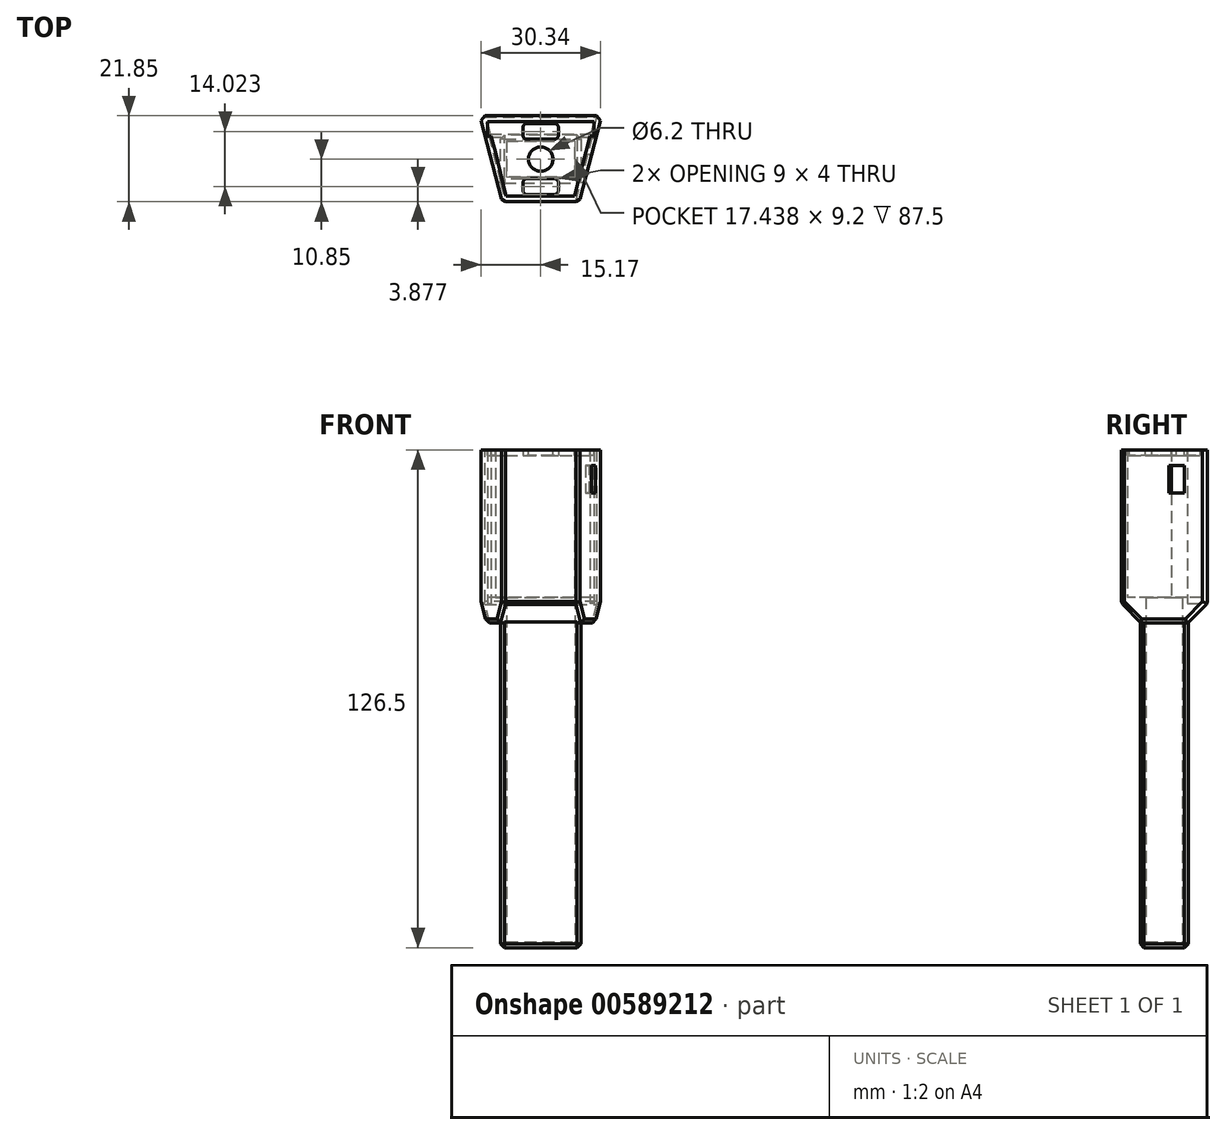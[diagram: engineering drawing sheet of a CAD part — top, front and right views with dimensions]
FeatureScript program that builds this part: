
annotation { "Feature Type Name" : "Feature", "Feature Type Description" : "" }
export const myFeature = defineFeature(function(context is Context, id is Id, definition is map)
    precondition{}
    {
        {
            var Q0;
            Q0=qCreatedBy(makeId("Top.planeOp"),FACE);
            var sketch = newSketch(context, id + "F0", { "sketchPlane" : qUnion([Q0])});
            skLineSegment(sketch, "E0", {"start": v(0, 11) * mm, "end": v(15.5, 11) * mm});
            skLineSegment(sketch, "E1", {"start": v(9.75, -10.85) * mm, "end": v(0, -10.85) * mm});
            skLineSegment(sketch, "E2", {"start": v(-9.75, -10.85) * mm, "end": v(0, -10.85) * mm});
            skLineSegment(sketch, "E3", {"start": v(-15.5, 11) * mm, "end": v(0, 11) * mm});
            skLineSegment(sketch, "E4", {"start": v(15.5, 11) * mm, "end": v(9.75, -10.85) * mm});
            skLineSegment(sketch, "E5", {"start": v(-15.5, 11) * mm, "end": v(-9.75, -10.85) * mm});
            skLineSegment(sketch, "E6", {"start": v(0, 9.5) * mm, "end": v(-15.1, 9.5) * mm});
            skLineSegment(sketch, "E7", {"start": v(0, 9.5) * mm, "end": v(15.1, 9.5) * mm});
            skLineSegment(sketch, "E8", {"start": v(0, -9.35) * mm, "end": v(-10.14, -9.35) * mm});
            skLineSegment(sketch, "E9", {"start": v(0, -9.35) * mm, "end": v(10.14, -9.35) * mm});
            skLineSegment(sketch, "E10", {"start": v(-11.54, 1.84) * mm, "end": v(-13.55, 9.5) * mm});
            skLineSegment(sketch, "E11", {"start": v(11.74, 2.61) * mm, "end": v(13.55, 9.5) * mm});
            skLineSegment(sketch, "E12", {"start": v(8.72, 0) * mm, "end": v(8.72, 4.6) * mm});
            skLineSegment(sketch, "E13", {"start": v(8.72, 4.6) * mm, "end": v(0, 4.6) * mm});
            skLineSegment(sketch, "E14.MirrorCS", {"start": v(-8.72, 0) * mm, "end": v(-8.72, 4.6) * mm});
            skLineSegment(sketch, "E15.MirrorCS", {"start": v(-8.72, 4.6) * mm, "end": v(0, 4.6) * mm});
            skLineSegment(sketch, "E16.MirrorCS", {"start": v(-8.72, 0) * mm, "end": v(-8.72, -4.6) * mm});
            skLineSegment(sketch, "E17.MirrorCS", {"start": v(-8.72, -4.6) * mm, "end": v(0, -4.6) * mm});
            skLineSegment(sketch, "E18.MirrorCS", {"start": v(8.72, -4.6) * mm, "end": v(0, -4.6) * mm});
            skLineSegment(sketch, "E19.MirrorCS", {"start": v(8.72, 0) * mm, "end": v(8.72, -4.6) * mm});
            skLineSegment(sketch, "E20", {"start": v(0, 4.6) * mm, "end": v(0, 6.1) * mm});
            skLineSegment(sketch, "E21", {"start": v(0, 6.1) * mm, "end": v(-8.72, 6.1) * mm});
            skLineSegment(sketch, "E22", {"start": v(-8.72, 6.1) * mm, "end": v(-10.22, 6.1) * mm});
            skLineSegment(sketch, "E23", {"start": v(-10.22, 6.1) * mm, "end": v(-10.22, -4.6) * mm});
            skLineSegment(sketch, "E24", {"start": v(-10.22, -4.6) * mm, "end": v(-10.22, -6.1) * mm});
            skLineSegment(sketch, "E25", {"start": v(0, 4.6) * mm, "end": v(0, 0) * mm, "construction": true});
            skLineSegment(sketch, "E26", {"start": v(0, 0) * mm, "end": v(-8.72, 0) * mm, "construction": true});
            skLineSegment(sketch, "E27", {"start": v(-10.22, -6.1) * mm, "end": v(0, -6.1) * mm});
            skLineSegment(sketch, "E28.MirrorCS", {"start": v(0, 6.1) * mm, "end": v(8.72, 6.1) * mm});
            skLineSegment(sketch, "E29.MirrorCS", {"start": v(8.72, 6.1) * mm, "end": v(10.22, 6.1) * mm});
            skLineSegment(sketch, "E30.MirrorCS", {"start": v(10.22, 6.1) * mm, "end": v(10.22, -4.6) * mm});
            skLineSegment(sketch, "E31.MirrorCS", {"start": v(10.22, -4.6) * mm, "end": v(10.22, -6.1) * mm});
            skLineSegment(sketch, "E32.MirrorCS", {"start": v(10.22, -6.1) * mm, "end": v(0, -6.1) * mm});
            skLineSegment(sketch, "E33", {"start": v(0, -4.6) * mm, "end": v(0, -9.35) * mm, "construction": true});
            skLineSegment(sketch, "E34", {"start": v(0, -6.97) * mm, "end": v(-4.5, -6.97) * mm, "construction": true});
            skLineSegment(sketch, "E35", {"start": v(-4.5, -6.97) * mm, "end": v(0, -6.97) * mm, "construction": true});
            skLineSegment(sketch, "E36", {"start": v(4.5, -6.97) * mm, "end": v(0, -6.97) * mm, "construction": true});
            skLineSegment(sketch, "E37", {"start": v(0, -6.97) * mm, "end": v(0, -8.97) * mm, "construction": true});
            skLineSegment(sketch, "E38", {"start": v(0, -8.97) * mm, "end": v(0, -6.97) * mm, "construction": true});
            skLineSegment(sketch, "E39", {"start": v(0, -6.97) * mm, "end": v(0, -4.97) * mm, "construction": true});
            skLineSegment(sketch, "E40", {"start": v(0, -4.97) * mm, "end": v(-3.5, -4.97) * mm});
            skLineSegment(sketch, "E41", {"start": v(-4.5, -5.97) * mm, "end": v(-4.5, -6.97) * mm});
            skLineSegment(sketch, "E42", {"start": v(-4.5, -7.97) * mm, "end": v(-4.5, -6.97) * mm});
            skLineSegment(sketch, "E43", {"start": v(0, -8.97) * mm, "end": v(-3.5, -8.97) * mm});
            skLineSegment(sketch, "E44.MirrorCS", {"start": v(0, -8.97) * mm, "end": v(3.5, -8.97) * mm});
            skLineSegment(sketch, "E45.MirrorCS", {"start": v(4.5, -7.97) * mm, "end": v(4.5, -6.97) * mm});
            skLineSegment(sketch, "E46.MirrorCS", {"start": v(0, -4.97) * mm, "end": v(3.5, -4.97) * mm});
            skLineSegment(sketch, "E47.MirrorCS", {"start": v(4.5, -5.97) * mm, "end": v(4.5, -6.97) * mm});
            skPoint(sketch, "E48.visualSharp", {"position": v(4.5, -4.97) * mm});
            skArc(sketch, "E48.filletArc", {"start": v(4.5, -5.97) * mm, "mid": v(4.2, -5.27) * mm, "end": v(3.5, -4.97) * mm});
            skPoint(sketch, "E49.visualSharp", {"position": v(4.5, -8.97) * mm});
            skArc(sketch, "E49.filletArc", {"start": v(3.5, -8.97) * mm, "mid": v(4.2, -8.68) * mm, "end": v(4.5, -7.97) * mm});
            skPoint(sketch, "E50.visualSharp", {"position": v(-4.5, -8.97) * mm});
            skArc(sketch, "E50.filletArc", {"start": v(-4.5, -7.97) * mm, "mid": v(-4.2, -8.68) * mm, "end": v(-3.5, -8.97) * mm});
            skPoint(sketch, "E51.visualSharp", {"position": v(-4.5, -4.97) * mm});
            skArc(sketch, "E51.filletArc", {"start": v(-3.5, -4.97) * mm, "mid": v(-4.2, -5.27) * mm, "end": v(-4.5, -5.97) * mm});
            skLineSegment(sketch, "E52", {"start": v(0, 4.6) * mm, "end": v(0, 9.5) * mm});
            skLineSegment(sketch, "E53", {"start": v(0, 7.05) * mm, "end": v(0, 4.6) * mm});
            skLineSegment(sketch, "E54", {"start": v(0, 9.5) * mm, "end": v(0, 4.6) * mm, "construction": true});
            skLineSegment(sketch, "E55", {"start": v(0, 7.05) * mm, "end": v(-4.5, 7.05) * mm, "construction": true});
            skLineSegment(sketch, "E56", {"start": v(-4.5, 7.05) * mm, "end": v(0, 7.05) * mm, "construction": true});
            skLineSegment(sketch, "E57", {"start": v(4.5, 7.05) * mm, "end": v(0, 7.05) * mm, "construction": true});
            skLineSegment(sketch, "E58", {"start": v(0, 7.05) * mm, "end": v(0, 5.05) * mm, "construction": true});
            skLineSegment(sketch, "E59", {"start": v(0, 5.05) * mm, "end": v(0, 7.05) * mm, "construction": true});
            skLineSegment(sketch, "E60", {"start": v(0, 7.05) * mm, "end": v(0, 9.05) * mm, "construction": true});
            skLineSegment(sketch, "E61", {"start": v(0, 9.05) * mm, "end": v(-3.5, 9.05) * mm});
            skLineSegment(sketch, "E62", {"start": v(-4.5, 8.05) * mm, "end": v(-4.5, 7.05) * mm});
            skLineSegment(sketch, "E63", {"start": v(-4.5, 6.05) * mm, "end": v(-4.5, 7.05) * mm});
            skLineSegment(sketch, "E64", {"start": v(0, 5.05) * mm, "end": v(-3.5, 5.05) * mm});
            skLineSegment(sketch, "E65.MirrorCS", {"start": v(0, 5.05) * mm, "end": v(3.5, 5.05) * mm});
            skLineSegment(sketch, "E66.MirrorCS", {"start": v(4.5, 6.05) * mm, "end": v(4.5, 7.05) * mm});
            skLineSegment(sketch, "E67.MirrorCS", {"start": v(0, 9.05) * mm, "end": v(3.5, 9.05) * mm});
            skLineSegment(sketch, "E68.MirrorCS", {"start": v(4.5, 8.05) * mm, "end": v(4.5, 7.05) * mm});
            skPoint(sketch, "E69.visualSharp", {"position": v(4.5, 9.05) * mm});
            skArc(sketch, "E69.filletArc", {"start": v(4.5, 8.05) * mm, "mid": v(4.2, 8.76) * mm, "end": v(3.5, 9.05) * mm});
            skPoint(sketch, "E70.visualSharp", {"position": v(4.5, 5.05) * mm});
            skArc(sketch, "E70.filletArc", {"start": v(3.5, 5.05) * mm, "mid": v(4.2, 5.34) * mm, "end": v(4.5, 6.05) * mm});
            skPoint(sketch, "E71.visualSharp", {"position": v(-4.5, 5.05) * mm});
            skArc(sketch, "E71.filletArc", {"start": v(-4.5, 6.05) * mm, "mid": v(-4.2, 5.34) * mm, "end": v(-3.5, 5.05) * mm});
            skPoint(sketch, "E72.visualSharp", {"position": v(-4.5, 9.05) * mm});
            skArc(sketch, "E72.filletArc", {"start": v(-3.5, 9.05) * mm, "mid": v(-4.2, 8.76) * mm, "end": v(-4.5, 8.05) * mm});
            skLineSegment(sketch, "E73", {"start": v(11.74, 2.61) * mm, "end": v(8.6, -9.35) * mm});
            skLineSegment(sketch, "E74", {"start": v(-11.54, 1.84) * mm, "end": v(-8.83, -9.35) * mm});
            skLineSegment(sketch, "E75", {"start": v(-11.53, 1.83) * mm, "end": v(-13, 1.47) * mm});
            skLineSegment(sketch, "E76", {"start": v(10.76, -1.1) * mm, "end": v(12.21, -1.49) * mm});
            skLineSegment(sketch, "E77", {"start": v(-14.14, 5.83) * mm, "end": v(-13.55, 5.83) * mm});
            skLineSegment(sketch, "E78", {"start": v(-13.55, 5.83) * mm, "end": v(-13.55, 9.5) * mm});
            skLineSegment(sketch, "E79", {"start": v(-13.55, 5.83) * mm, "end": v(-12.59, 5.83) * mm});
            skLineSegment(sketch, "E80.MirrorCS", {"start": v(13.55, 5.83) * mm, "end": v(13.55, 9.5) * mm});
            skLineSegment(sketch, "E81.MirrorCS", {"start": v(13.55, 5.83) * mm, "end": v(12.59, 5.83) * mm});
            skSolve(sketch);
        }
        {
            var Q0;
            Q0 = qSketchRegion(id + "F0", true);
            var Q1;
            {var subQ5=sQuery(id+"F0.wireOp",EDGE,"E24");Q1=makeQuery(id+"F0.imprint","IMPRINT",FACE,{"disambiguationData":[TD([[makeQuery(id+"F0.imprint","IMPRINT",EDGE,{"derivedFrom":subQ5}),1.0]])]});}
            var Q2;
            {var subQ5=sQuery(id+"F0.wireOp",EDGE,"E31.MirrorCS");Q2=makeQuery(id+"F0.imprint","IMPRINT",FACE,{"disambiguationData":[TD([[makeQuery(id+"F0.imprint","IMPRINT",EDGE,{"derivedFrom":subQ5}),-1.0]])]});}
            extrude(context, id + "F1", {"entities" : qUnion([Q0, Q1, Q2]), "depth" : 39 * mm, "offsetDistance" : 25 * mm});
        }
        {
            var Q0;
            {var subQ9=sQuery(id+"F0.wireOp",EDGE,"E10");Q0=makeQuery(id+"F0.imprint","IMPRINT",FACE,{"disambiguationData":[TD([[makeQuery(id+"F0.imprint","IMPRINT",EDGE,{"derivedFrom":subQ9}),-1.0]])]});}
            var Q1;
            {var subQ1=sQuery(id+"F0.wireOp",EDGE,"E9");var subQ5=sQuery(id+"F0.wireOp",EDGE,"E8");var subQ6=makeQuery(id+"F0.imprint","INTERSECT",VERTEX,{"derivedFrom":[subQ5,subQ1]});Q1=makeQuery(id+"F0.imprint","IMPRINT",FACE,{"disambiguationData":[TD([[makeQuery(id+"F0.imprint","IMPRINT",EDGE,{"disambiguationData":[TD([[subQ6,-1.0]])],"derivedFrom":subQ5}),-1.0]])]});}
            var Q2;
            {var subQ8=sQuery(id+"F0.wireOp",EDGE,"E11");Q2=makeQuery(id+"F0.imprint","IMPRINT",FACE,{"disambiguationData":[TD([[makeQuery(id+"F0.imprint","IMPRINT",EDGE,{"derivedFrom":subQ8}),1.0]])]});}
            var Q3;
            {var subQ7=sQuery(id+"F0.wireOp",EDGE,"E67.MirrorCS");Q3=makeQuery(id+"F0.imprint","IMPRINT",FACE,{"disambiguationData":[TD([[makeQuery(id+"F0.imprint","IMPRINT",EDGE,{"derivedFrom":subQ7}),-1.0]])]});}
            var Q4;
            {var subQ0=sQuery(id+"F0.wireOp",EDGE,"E61");Q4=makeQuery(id+"F0.imprint","IMPRINT",FACE,{"disambiguationData":[TD([[makeQuery(id+"F0.imprint","IMPRINT",EDGE,{"derivedFrom":subQ0}),1.0]])]});}
            var Q5;
            {var subQ0=sQuery(id+"F0.wireOp",EDGE,"E42");Q5=makeQuery(id+"F0.imprint","IMPRINT",FACE,{"disambiguationData":[TD([[makeQuery(id+"F0.imprint","IMPRINT",EDGE,{"derivedFrom":subQ0}),-1.0]])]});}
            var Q6;
            Q6=makeQuery(id+"F0.imprint","IMPRINT",FACE,{"disambiguationData":[TD([[makeQuery(id+"F0.imprint","IMPRINT",EDGE,{"derivedFrom":sQuery(id+"F0.wireOp",EDGE,"E12")}),-1.0]])]});
            var Q7;
            Q7=makeQuery(id+"F0.imprint","IMPRINT",FACE,{"disambiguationData":[TD([[makeQuery(id+"F0.imprint","IMPRINT",EDGE,{"derivedFrom":sQuery(id+"F0.wireOp",EDGE,"E40")}),1.0]])]});
            var Q8;
            {var subQ4=sQuery(id+"F0.wireOp",EDGE,"E64");Q8=makeQuery(id+"F0.imprint","IMPRINT",FACE,{"disambiguationData":[TD([[makeQuery(id+"F0.imprint","IMPRINT",EDGE,{"derivedFrom":subQ4}),-1.0]])]});}
            var Q9;
            {var subQ6=sQuery(id+"F0.wireOp",EDGE,"E65.MirrorCS");Q9=makeQuery(id+"F0.imprint","IMPRINT",FACE,{"disambiguationData":[TD([[makeQuery(id+"F0.imprint","IMPRINT",EDGE,{"derivedFrom":subQ6}),1.0]])]});}
            extrude(context, id + "F2", {"entities" : qUnion([Q0, Q1, Q2, Q3, Q4, Q5, Q6, Q7, Q8, Q9]), "operationType" : NewBodyOperationType.ADD, "depth" : 1.5 * mm, "offsetDistance" : 25 * mm});
        }
        {
            var Q0;
            Q0=makeQuery(id+"F1.opExtrude","CAP_FACE",FACE,{"disambiguationData":[OSD([sQuery(id+"F0.wireOp",EDGE,"E0"),sQuery(id+"F0.wireOp",EDGE,"E1"),sQuery(id+"F0.wireOp",EDGE,"E2"),sQuery(id+"F0.wireOp",EDGE,"E3"),sQuery(id+"F0.wireOp",EDGE,"E4"),sQuery(id+"F0.wireOp",EDGE,"E5"),sQuery(id+"F0.wireOp",EDGE,"E6"),sQuery(id+"F0.wireOp",EDGE,"E7"),sQuery(id+"F0.wireOp",EDGE,"E8"),sQuery(id+"F0.wireOp",EDGE,"E9"),sQuery(id+"F0.wireOp",EDGE,"E10"),sQuery(id+"F0.wireOp",EDGE,"pa9DFjsO-60TX-mNzs-XNHe-tOrfid2OEU49"),sQuery(id+"F0.wireOp",EDGE,"E11"),sQuery(id+"F0.wireOp",EDGE,"UQAgsL2E-6xYK-50WF-40Pj-b5XUAbo4wAtb")])],"isStart":false});
            var sketch = newSketch(context, id + "F3", { "sketchPlane" : qUnion([Q0])});
            skSolve(sketch);
        }
        {
            var Q0;
            {var subQ0=sQuery(id+"F0.wireOp",EDGE,"pa9DFjsO-60TX-mNzs-XNHe-tOrfid2OEU49");Q0=makeQuery(id+"F3.imprint","IMPRINT",FACE,{"disambiguationData":[TD([[makeQuery(id+"F3.imprint","IMPRINT",EDGE,{"derivedFrom":makeQuery(id+"F1.opExtrude","CAP_EDGE",EDGE,{"disambiguationData":[OSD([subQ0])],"isStart":false})}),1.0]])]});}
            var Q1;
            Q1=makeQuery(id+"F3.imprint","IMPRINT",FACE,{"disambiguationData":[TD([[makeQuery(id+"F3.imprint","IMPRINT",EDGE,{"derivedFrom":makeQuery(id+"F1.opExtrude","CAP_EDGE",EDGE,{"disambiguationData":[OSD([sQuery(id+"F0.wireOp",EDGE,"E10")])],"isStart":false})}),-1.0]])]});
            extrude(context, id + "F4", {"entities" : qUnion([Q0, Q1]), "oppositeDirection" : true, "depth" : 1.5 * mm, "offsetDistance" : 25 * mm});
        }
        {
            var Q0;
            {var subQ5=sQuery(id+"F0.wireOp",EDGE,"E24");Q0=makeQuery(id+"F0.imprint","IMPRINT",FACE,{"disambiguationData":[TD([[makeQuery(id+"F0.imprint","IMPRINT",EDGE,{"derivedFrom":subQ5}),1.0]])]});}
            var Q1;
            {var subQ5=sQuery(id+"F0.wireOp",EDGE,"E31.MirrorCS");Q1=makeQuery(id+"F0.imprint","IMPRINT",FACE,{"disambiguationData":[TD([[makeQuery(id+"F0.imprint","IMPRINT",EDGE,{"derivedFrom":subQ5}),-1.0]])]});}
            var Q2;
            Q2=makeQuery(id+"F0.imprint","IMPRINT",FACE,{"disambiguationData":[TD([[makeQuery(id+"F0.imprint","IMPRINT",EDGE,{"derivedFrom":sQuery(id+"F0.wireOp",EDGE,"E12")}),-1.0]])]});
            var Q3;
            {var subQ4=sQuery(id+"F0.wireOp",EDGE,"E64");Q3=makeQuery(id+"F0.imprint","IMPRINT",FACE,{"disambiguationData":[TD([[makeQuery(id+"F0.imprint","IMPRINT",EDGE,{"derivedFrom":subQ4}),-1.0]])]});}
            var Q4;
            Q4=makeQuery(id+"F0.imprint","IMPRINT",FACE,{"disambiguationData":[TD([[makeQuery(id+"F0.imprint","IMPRINT",EDGE,{"derivedFrom":sQuery(id+"F0.wireOp",EDGE,"E40")}),1.0]])]});
            var Q5;
            {var subQ6=sQuery(id+"F0.wireOp",EDGE,"E65.MirrorCS");Q5=makeQuery(id+"F0.imprint","IMPRINT",FACE,{"disambiguationData":[TD([[makeQuery(id+"F0.imprint","IMPRINT",EDGE,{"derivedFrom":subQ6}),1.0]])]});}
            extrude(context, id + "F5", {"entities" : qUnion([Q0, Q1, Q2, Q3, Q4, Q5]), "oppositeDirection" : true, "depth" : 87.5 * mm, "offsetDistance" : 25 * mm});
        }
        {
            var Q0;
            Q0=makeQuery(id+"F5.opExtrude","CAP_FACE",FACE,{"disambiguationData":[OSD([sQuery(id+"F0.wireOp",EDGE,"E12"),sQuery(id+"F0.wireOp",EDGE,"E13"),sQuery(id+"F0.wireOp",EDGE,"E14.MirrorCS"),sQuery(id+"F0.wireOp",EDGE,"E15.MirrorCS"),sQuery(id+"F0.wireOp",EDGE,"E16.MirrorCS"),sQuery(id+"F0.wireOp",EDGE,"E17.MirrorCS"),sQuery(id+"F0.wireOp",EDGE,"E18.MirrorCS"),sQuery(id+"F0.wireOp",EDGE,"E19.MirrorCS"),sQuery(id+"F0.wireOp",EDGE,"E21"),sQuery(id+"F0.wireOp",EDGE,"E22"),sQuery(id+"F0.wireOp",EDGE,"E23"),sQuery(id+"F0.wireOp",EDGE,"E24"),sQuery(id+"F0.wireOp",EDGE,"E27"),sQuery(id+"F0.wireOp",EDGE,"E28.MirrorCS"),sQuery(id+"F0.wireOp",EDGE,"E29.MirrorCS"),sQuery(id+"F0.wireOp",EDGE,"E30.MirrorCS"),sQuery(id+"F0.wireOp",EDGE,"E31.MirrorCS"),sQuery(id+"F0.wireOp",EDGE,"E32.MirrorCS")])],"isStart":false});
            var sketch = newSketch(context, id + "F6", { "sketchPlane" : qUnion([Q0])});
            skSolve(sketch);
        }
        {
            var Q0;
            Q0=makeQuery(id+"F6.imprint","IMPRINT",FACE,{"disambiguationData":[TD([[makeQuery(id+"F6.imprint","IMPRINT",EDGE,{"derivedFrom":makeQuery(id+"F5.opExtrude","CAP_EDGE",EDGE,{"disambiguationData":[OSD([sQuery(id+"F0.wireOp",EDGE,"E12"),sQuery(id+"F0.wireOp",EDGE,"E19.MirrorCS")])],"isStart":false})}),-1.0]])]});
            extrude(context, id + "F7", {"entities" : qUnion([Q0]), "operationType" : NewBodyOperationType.ADD, "oppositeDirection" : true, "depth" : 1.5 * mm, "offsetDistance" : 25 * mm});
        }
        {
            var Q0;
            {var subQ1=sQuery(id+"F0.wireOp",EDGE,"E9");var subQ5=sQuery(id+"F0.wireOp",EDGE,"E8");var subQ6=makeQuery(id+"F0.imprint","INTERSECT",VERTEX,{"derivedFrom":[subQ5,subQ1]});Q0=makeQuery(id+"F0.imprint","IMPRINT",FACE,{"disambiguationData":[TD([[makeQuery(id+"F0.imprint","IMPRINT",EDGE,{"disambiguationData":[TD([[subQ6,-1.0]])],"derivedFrom":subQ5}),-1.0]])]});}
            var Q1;
            {var subQ5=sQuery(id+"F0.wireOp",EDGE,"E1");Q1=makeQuery(id+"F0.imprint","IMPRINT",FACE,{"disambiguationData":[TD([[makeQuery(id+"F0.imprint","IMPRINT",EDGE,{"derivedFrom":subQ5}),-1.0]])]});}
            var Q2;
            {var subQ0=sQuery(id+"F0.wireOp",EDGE,"E11");Q2=makeQuery(id+"F0.imprint","IMPRINT",FACE,{"disambiguationData":[TD([[makeQuery(id+"F0.imprint","IMPRINT",EDGE,{"derivedFrom":subQ0}),-1.0]])]});}
            var Q3;
            {var subQ8=sQuery(id+"F0.wireOp",EDGE,"E10");Q3=makeQuery(id+"F0.imprint","IMPRINT",FACE,{"disambiguationData":[TD([[makeQuery(id+"F0.imprint","IMPRINT",EDGE,{"derivedFrom":subQ8}),-1.0]])]});}
            var Q4;
            {var subQ5=sQuery(id+"F0.wireOp",EDGE,"E0");Q4=makeQuery(id+"F0.imprint","IMPRINT",FACE,{"disambiguationData":[TD([[makeQuery(id+"F0.imprint","IMPRINT",EDGE,{"derivedFrom":subQ5}),-1.0]])]});}
            var Q5;
            {var subQ0=sQuery(id+"F0.wireOp",EDGE,"E42");Q5=makeQuery(id+"F0.imprint","IMPRINT",FACE,{"disambiguationData":[TD([[makeQuery(id+"F0.imprint","IMPRINT",EDGE,{"derivedFrom":subQ0}),-1.0]])]});}
            var Q6;
            {var subQ5=sQuery(id+"F0.wireOp",EDGE,"E11");Q6=makeQuery(id+"F0.imprint","IMPRINT",FACE,{"disambiguationData":[TD([[makeQuery(id+"F0.imprint","IMPRINT",EDGE,{"derivedFrom":subQ5}),1.0]])]});}
            var Q7;
            {var subQ7=sQuery(id+"F0.wireOp",EDGE,"E67.MirrorCS");Q7=makeQuery(id+"F0.imprint","IMPRINT",FACE,{"disambiguationData":[TD([[makeQuery(id+"F0.imprint","IMPRINT",EDGE,{"derivedFrom":subQ7}),-1.0]])]});}
            var Q8;
            {var subQ0=sQuery(id+"F0.wireOp",EDGE,"E61");Q8=makeQuery(id+"F0.imprint","IMPRINT",FACE,{"disambiguationData":[TD([[makeQuery(id+"F0.imprint","IMPRINT",EDGE,{"derivedFrom":subQ0}),1.0]])]});}
            var Q9;
            {var subQ0=sQuery(id+"F0.wireOp",EDGE,"E24");Q9=makeQuery(id+"F0.imprint","IMPRINT",FACE,{"disambiguationData":[TD([[makeQuery(id+"F0.imprint","IMPRINT",EDGE,{"derivedFrom":subQ0}),-1.0]])]});}
            var Q10;
            {var subQ0=sQuery(id+"F0.wireOp",EDGE,"E31.MirrorCS");Q10=makeQuery(id+"F0.imprint","IMPRINT",FACE,{"disambiguationData":[TD([[makeQuery(id+"F0.imprint","IMPRINT",EDGE,{"derivedFrom":subQ0}),1.0]])]});}
            var Q11;
            {var subQ0=sQuery(id+"F0.wireOp",EDGE,"E78");Q11=makeQuery(id+"F0.imprint","IMPRINT",FACE,{"disambiguationData":[TD([[makeQuery(id+"F0.imprint","IMPRINT",EDGE,{"derivedFrom":subQ0}),-1.0]])]});}
            var Q12;
            {var subQ0=sQuery(id+"F0.wireOp",EDGE,"E31.MirrorCS");Q12=makeQuery(id+"F0.imprint","IMPRINT",FACE,{"disambiguationData":[TD([[makeQuery(id+"F0.imprint","IMPRINT",EDGE,{"derivedFrom":subQ0}),-1.0]])]});}
            var Q13;
            {var subQ0=sQuery(id+"F0.wireOp",EDGE,"E24");Q13=makeQuery(id+"F0.imprint","IMPRINT",FACE,{"disambiguationData":[TD([[makeQuery(id+"F0.imprint","IMPRINT",EDGE,{"derivedFrom":subQ0}),1.0]])]});}
            var Q14;
            {var subQ3=sQuery(id+"F0.wireOp",EDGE,"E75");Q14=makeQuery(id+"F0.imprint","IMPRINT",FACE,{"disambiguationData":[TD([[makeQuery(id+"F0.imprint","IMPRINT",EDGE,{"derivedFrom":subQ3}),-1.0]])]});}
            var Q15;
            {var subQ3=sQuery(id+"F0.wireOp",EDGE,"E77");Q15=makeQuery(id+"F0.imprint","IMPRINT",FACE,{"disambiguationData":[TD([[makeQuery(id+"F0.imprint","IMPRINT",EDGE,{"derivedFrom":subQ3}),1.0]])]});}
            var Q16;
            {var subQ3=sQuery(id+"F0.wireOp",EDGE,"E76");Q16=makeQuery(id+"F0.imprint","IMPRINT",FACE,{"disambiguationData":[TD([[makeQuery(id+"F0.imprint","IMPRINT",EDGE,{"derivedFrom":subQ3}),1.0]])]});}
            extrude(context, id + "F8", {"entities" : qUnion([Q0, Q1, Q2, Q3, Q4, Q5, Q6, Q7, Q8, Q9, Q10, Q11, Q12, Q13, Q14, Q15, Q16]), "operationType" : NewBodyOperationType.ADD, "oppositeDirection" : true, "depth" : 5 * mm, "offsetDistance" : 25 * mm});
        }
        {
            var Q0;
            Q0=makeQuery(id+"F8.opExtrude","CAP_EDGE",EDGE,{"disambiguationData":[OSD([sQuery(id+"F0.wireOp",EDGE,"E1"),sQuery(id+"F0.wireOp",EDGE,"E2")])],"isStart":false});
            var Q1;
            Q1=makeQuery(id+"F8.opExtrude","CAP_EDGE",EDGE,{"disambiguationData":[OSD([sQuery(id+"F0.wireOp",EDGE,"E0"),sQuery(id+"F0.wireOp",EDGE,"E3")])],"isStart":false});
            chamfer(context, id + "F9", {"entities" : qUnion([Q0, Q1]), "width" : 5 * mm, "tangentPropagation" : true});
        }
        {
            var Q0;
            {var subQ0=sQuery(id+"F0.wireOp",EDGE,"E42");Q0=makeQuery(id+"F0.imprint","IMPRINT",FACE,{"disambiguationData":[TD([[makeQuery(id+"F0.imprint","IMPRINT",EDGE,{"derivedFrom":subQ0}),-1.0]])]});}
            var Q1;
            Q1=makeQuery(id+"F0.imprint","IMPRINT",FACE,{"disambiguationData":[TD([[makeQuery(id+"F0.imprint","IMPRINT",EDGE,{"derivedFrom":sQuery(id+"F0.wireOp",EDGE,"E40")}),1.0]])]});
            var Q2;
            {var subQ6=sQuery(id+"F0.wireOp",EDGE,"E65.MirrorCS");Q2=makeQuery(id+"F0.imprint","IMPRINT",FACE,{"disambiguationData":[TD([[makeQuery(id+"F0.imprint","IMPRINT",EDGE,{"derivedFrom":subQ6}),1.0]])]});}
            var Q3;
            {var subQ4=sQuery(id+"F0.wireOp",EDGE,"E64");Q3=makeQuery(id+"F0.imprint","IMPRINT",FACE,{"disambiguationData":[TD([[makeQuery(id+"F0.imprint","IMPRINT",EDGE,{"derivedFrom":subQ4}),-1.0]])]});}
            var Q4;
            {var subQ7=sQuery(id+"F0.wireOp",EDGE,"E67.MirrorCS");Q4=makeQuery(id+"F0.imprint","IMPRINT",FACE,{"disambiguationData":[TD([[makeQuery(id+"F0.imprint","IMPRINT",EDGE,{"derivedFrom":subQ7}),-1.0]])]});}
            var Q5;
            {var subQ0=sQuery(id+"F0.wireOp",EDGE,"E61");Q5=makeQuery(id+"F0.imprint","IMPRINT",FACE,{"disambiguationData":[TD([[makeQuery(id+"F0.imprint","IMPRINT",EDGE,{"derivedFrom":subQ0}),1.0]])]});}
            extrude(context, id + "F10", {"entities" : qUnion([Q0, Q1, Q2, Q3, Q4, Q5]), "operationType" : NewBodyOperationType.REMOVE, "depth" : 40 * mm, "offsetDistance" : 25 * mm});
        }
        {
            var Q0;
            Q0=makeQuery(id+"F5.opExtrude","SWEPT_EDGE",EDGE,{"disambiguationData":[OSD([sQuery(id+"F0.wireOp",EDGE,"E31.MirrorCS"),sQuery(id+"F0.wireOp",EDGE,"E32.MirrorCS")])]});
            var Q1;
            Q1=makeQuery(id+"F5.opExtrude","SWEPT_EDGE",EDGE,{"disambiguationData":[OSD([sQuery(id+"F0.wireOp",EDGE,"E24"),sQuery(id+"F0.wireOp",EDGE,"E27")])]});
            var Q2;
            Q2=makeQuery(id+"F5.opExtrude","SWEPT_EDGE",EDGE,{"disambiguationData":[OSD([sQuery(id+"F0.wireOp",EDGE,"E22"),sQuery(id+"F0.wireOp",EDGE,"E23")])]});
            var Q3;
            Q3=makeQuery(id+"F5.opExtrude","SWEPT_EDGE",EDGE,{"disambiguationData":[OSD([sQuery(id+"F0.wireOp",EDGE,"E29.MirrorCS"),sQuery(id+"F0.wireOp",EDGE,"E30.MirrorCS")])]});
            var Q4;
            Q4=makeQuery(id+"F5.opExtrude","CAP_EDGE",EDGE,{"disambiguationData":[OSD([sQuery(id+"F0.wireOp",EDGE,"E27"),sQuery(id+"F0.wireOp",EDGE,"E32.MirrorCS")])],"isStart":false});
            var Q5;
            Q5=makeQuery(id+"F5.opExtrude","CAP_EDGE",EDGE,{"disambiguationData":[OSD([sQuery(id+"F0.wireOp",EDGE,"E23"),sQuery(id+"F0.wireOp",EDGE,"E24")])],"isStart":false});
            var Q6;
            Q6=makeQuery(id+"F5.opExtrude","CAP_EDGE",EDGE,{"disambiguationData":[OSD([sQuery(id+"F0.wireOp",EDGE,"E21"),sQuery(id+"F0.wireOp",EDGE,"E22"),sQuery(id+"F0.wireOp",EDGE,"E28.MirrorCS"),sQuery(id+"F0.wireOp",EDGE,"E29.MirrorCS")])],"isStart":false});
            var Q7;
            Q7=makeQuery(id+"F5.opExtrude","CAP_EDGE",EDGE,{"disambiguationData":[OSD([sQuery(id+"F0.wireOp",EDGE,"E30.MirrorCS"),sQuery(id+"F0.wireOp",EDGE,"E31.MirrorCS")])],"isStart":false});
            chamfer(context, id + "F11", {"entities" : qUnion([Q0, Q1, Q2, Q3, Q4, Q5, Q6, Q7]), "width" : 1 * mm, "tangentPropagation" : true});
        }
        {
            var Q0;
            {var subQ0=sQuery(id+"F0.wireOp",EDGE,"E5");Q0=makeQuery(id+"F9.opChamfer","BLEND_EDGE",EDGE,{"blendedFrom":[makeQuery(id+"F8.opExtrude","CAP_EDGE",EDGE,{"disambiguationData":[OSD([sQuery(id+"F0.wireOp",EDGE,"E0"),sQuery(id+"F0.wireOp",EDGE,"E3")])],"isStart":false}),makeQuery(id+"F8.boolean.opBoolean","MERGE",FACE,{"derivedFrom":[makeQuery(id+"F1.opExtrude","SWEPT_FACE",FACE,{"disambiguationData":[OSD([subQ0])]}),makeQuery(id+"F8.opExtrude","SWEPT_FACE",FACE,{"disambiguationData":[OSD([subQ0])]})]})],"blendedInto":[makeQuery(id+"F8.boolean.opBoolean","MERGE",FACE,{"derivedFrom":[makeQuery(id+"F1.opExtrude","SWEPT_FACE",FACE,{"disambiguationData":[OSD([subQ0])]}),makeQuery(id+"F8.opExtrude","SWEPT_FACE",FACE,{"disambiguationData":[OSD([subQ0])]})]})]});}
            var Q1;
            {var subQ0=sQuery(id+"F0.wireOp",EDGE,"E5");Q1=makeQuery(id+"F9.opChamfer","BLEND_EDGE",EDGE,{"blendedFrom":[makeQuery(id+"F8.opExtrude","CAP_EDGE",EDGE,{"disambiguationData":[OSD([sQuery(id+"F0.wireOp",EDGE,"E1"),sQuery(id+"F0.wireOp",EDGE,"E2")])],"isStart":false}),makeQuery(id+"F8.boolean.opBoolean","MERGE",FACE,{"derivedFrom":[makeQuery(id+"F1.opExtrude","SWEPT_FACE",FACE,{"disambiguationData":[OSD([subQ0])]}),makeQuery(id+"F8.opExtrude","SWEPT_FACE",FACE,{"disambiguationData":[OSD([subQ0])]})]})],"blendedInto":[makeQuery(id+"F8.boolean.opBoolean","MERGE",FACE,{"derivedFrom":[makeQuery(id+"F1.opExtrude","SWEPT_FACE",FACE,{"disambiguationData":[OSD([subQ0])]}),makeQuery(id+"F8.opExtrude","SWEPT_FACE",FACE,{"disambiguationData":[OSD([subQ0])]})]})]});}
            var Q2;
            {var subQ0=sQuery(id+"F0.wireOp",EDGE,"E4");Q2=makeQuery(id+"F9.opChamfer","BLEND_EDGE",EDGE,{"blendedFrom":[makeQuery(id+"F8.opExtrude","CAP_EDGE",EDGE,{"disambiguationData":[OSD([sQuery(id+"F0.wireOp",EDGE,"E0"),sQuery(id+"F0.wireOp",EDGE,"E3")])],"isStart":false}),makeQuery(id+"F8.boolean.opBoolean","MERGE",FACE,{"derivedFrom":[makeQuery(id+"F1.opExtrude","SWEPT_FACE",FACE,{"disambiguationData":[OSD([subQ0])]}),makeQuery(id+"F8.opExtrude","SWEPT_FACE",FACE,{"disambiguationData":[OSD([subQ0])]})]})],"blendedInto":[makeQuery(id+"F8.boolean.opBoolean","MERGE",FACE,{"derivedFrom":[makeQuery(id+"F1.opExtrude","SWEPT_FACE",FACE,{"disambiguationData":[OSD([subQ0])]}),makeQuery(id+"F8.opExtrude","SWEPT_FACE",FACE,{"disambiguationData":[OSD([subQ0])]})]})]});}
            var Q3;
            {var subQ0=sQuery(id+"F0.wireOp",EDGE,"E4");Q3=makeQuery(id+"F9.opChamfer","BLEND_EDGE",EDGE,{"blendedFrom":[makeQuery(id+"F8.opExtrude","CAP_EDGE",EDGE,{"disambiguationData":[OSD([sQuery(id+"F0.wireOp",EDGE,"E1"),sQuery(id+"F0.wireOp",EDGE,"E2")])],"isStart":false}),makeQuery(id+"F8.boolean.opBoolean","MERGE",FACE,{"derivedFrom":[makeQuery(id+"F1.opExtrude","SWEPT_FACE",FACE,{"disambiguationData":[OSD([subQ0])]}),makeQuery(id+"F8.opExtrude","SWEPT_FACE",FACE,{"disambiguationData":[OSD([subQ0])]})]})],"blendedInto":[makeQuery(id+"F8.boolean.opBoolean","MERGE",FACE,{"derivedFrom":[makeQuery(id+"F1.opExtrude","SWEPT_FACE",FACE,{"disambiguationData":[OSD([subQ0])]}),makeQuery(id+"F8.opExtrude","SWEPT_FACE",FACE,{"disambiguationData":[OSD([subQ0])]})]})]});}
            var Q4;
            Q4=makeQuery(id+"F8.opExtrude","CAP_EDGE",EDGE,{"disambiguationData":[OSD([sQuery(id+"F0.wireOp",EDGE,"E4")])],"isStart":false});
            var Q5;
            Q5=makeQuery(id+"F8.opExtrude","CAP_EDGE",EDGE,{"disambiguationData":[OSD([sQuery(id+"F0.wireOp",EDGE,"E5")])],"isStart":false});
            var Q6;
            {var subQ0=sQuery(id+"F0.wireOp",EDGE,"E3");var subQ1=sQuery(id+"F0.wireOp",EDGE,"E0");Q6=makeQuery(id+"F9.opChamfer","BLEND_EDGE",EDGE,{"disambiguationData":[OD(1.0)],"blendedFrom":[makeQuery(id+"F8.opExtrude","CAP_EDGE",EDGE,{"disambiguationData":[OSD([subQ1,subQ0])],"isStart":false}),makeQuery(id+"F8.opExtrude","CAP_FACE",FACE,{"disambiguationData":[OSD([subQ1,sQuery(id+"F0.wireOp",EDGE,"E1"),sQuery(id+"F0.wireOp",EDGE,"E2"),subQ0,sQuery(id+"F0.wireOp",EDGE,"E4"),sQuery(id+"F0.wireOp",EDGE,"E5"),sQuery(id+"F0.wireOp",EDGE,"E21"),sQuery(id+"F0.wireOp",EDGE,"E22"),sQuery(id+"F0.wireOp",EDGE,"E23"),sQuery(id+"F0.wireOp",EDGE,"E24"),sQuery(id+"F0.wireOp",EDGE,"E27"),sQuery(id+"F0.wireOp",EDGE,"E28.MirrorCS"),sQuery(id+"F0.wireOp",EDGE,"E29.MirrorCS"),sQuery(id+"F0.wireOp",EDGE,"E30.MirrorCS"),sQuery(id+"F0.wireOp",EDGE,"E31.MirrorCS"),sQuery(id+"F0.wireOp",EDGE,"E32.MirrorCS")])],"isStart":false})],"blendedInto":[makeQuery(id+"F8.opExtrude","CAP_FACE",FACE,{"disambiguationData":[OSD([subQ1,sQuery(id+"F0.wireOp",EDGE,"E1"),sQuery(id+"F0.wireOp",EDGE,"E2"),subQ0,sQuery(id+"F0.wireOp",EDGE,"E4"),sQuery(id+"F0.wireOp",EDGE,"E5"),sQuery(id+"F0.wireOp",EDGE,"E21"),sQuery(id+"F0.wireOp",EDGE,"E22"),sQuery(id+"F0.wireOp",EDGE,"E23"),sQuery(id+"F0.wireOp",EDGE,"E24"),sQuery(id+"F0.wireOp",EDGE,"E27"),sQuery(id+"F0.wireOp",EDGE,"E28.MirrorCS"),sQuery(id+"F0.wireOp",EDGE,"E29.MirrorCS"),sQuery(id+"F0.wireOp",EDGE,"E30.MirrorCS"),sQuery(id+"F0.wireOp",EDGE,"E31.MirrorCS"),sQuery(id+"F0.wireOp",EDGE,"E32.MirrorCS")])],"isStart":false})]});}
            var Q7;
            {var subQ0=sQuery(id+"F0.wireOp",EDGE,"E3");var subQ1=sQuery(id+"F0.wireOp",EDGE,"E0");Q7=makeQuery(id+"F9.opChamfer","BLEND_EDGE",EDGE,{"blendedFrom":[makeQuery(id+"F8.opExtrude","CAP_EDGE",EDGE,{"disambiguationData":[OSD([subQ1,subQ0])],"isStart":false}),makeQuery(id+"F8.boolean.opBoolean","MERGE",FACE,{"derivedFrom":[makeQuery(id+"F1.opExtrude","SWEPT_FACE",FACE,{"disambiguationData":[OSD([subQ1,subQ0])]}),makeQuery(id+"F8.opExtrude","SWEPT_FACE",FACE,{"disambiguationData":[OSD([subQ1,subQ0])]})]})],"blendedInto":[makeQuery(id+"F8.boolean.opBoolean","MERGE",FACE,{"derivedFrom":[makeQuery(id+"F1.opExtrude","SWEPT_FACE",FACE,{"disambiguationData":[OSD([subQ1,subQ0])]}),makeQuery(id+"F8.opExtrude","SWEPT_FACE",FACE,{"disambiguationData":[OSD([subQ1,subQ0])]})]})]});}
            var Q8;
            {var subQ0=sQuery(id+"F0.wireOp",EDGE,"E2");var subQ1=sQuery(id+"F0.wireOp",EDGE,"E1");Q8=makeQuery(id+"F9.opChamfer","BLEND_EDGE",EDGE,{"blendedFrom":[makeQuery(id+"F8.opExtrude","CAP_EDGE",EDGE,{"disambiguationData":[OSD([subQ1,subQ0])],"isStart":false}),makeQuery(id+"F8.boolean.opBoolean","MERGE",FACE,{"derivedFrom":[makeQuery(id+"F1.opExtrude","SWEPT_FACE",FACE,{"disambiguationData":[OSD([subQ1,subQ0])]}),makeQuery(id+"F8.opExtrude","SWEPT_FACE",FACE,{"disambiguationData":[OSD([subQ1,subQ0])]})]})],"blendedInto":[makeQuery(id+"F8.boolean.opBoolean","MERGE",FACE,{"derivedFrom":[makeQuery(id+"F1.opExtrude","SWEPT_FACE",FACE,{"disambiguationData":[OSD([subQ1,subQ0])]}),makeQuery(id+"F8.opExtrude","SWEPT_FACE",FACE,{"disambiguationData":[OSD([subQ1,subQ0])]})]})]});}
            chamfer(context, id + "F12", {"entities" : qUnion([Q0, Q1, Q2, Q3, Q4, Q5, Q6, Q7, Q8]), "width" : 1 * mm, "tangentPropagation" : true});
        }
        {
            var Q0;
            {var subQ0=sQuery(id+"F0.wireOp",EDGE,"E4");var subQ1=sQuery(id+"F0.wireOp",EDGE,"E1");Q0=makeQuery(id+"F8.boolean.opBoolean","MERGE",EDGE,{"derivedFrom":[makeQuery(id+"F1.opExtrude","SWEPT_EDGE",EDGE,{"disambiguationData":[OSD([subQ1,subQ0])]}),makeQuery(id+"F8.opExtrude","SWEPT_EDGE",EDGE,{"disambiguationData":[OSD([subQ1,subQ0])]})]});}
            var Q1;
            {var subQ0=sQuery(id+"F0.wireOp",EDGE,"E5");var subQ1=sQuery(id+"F0.wireOp",EDGE,"E2");Q1=makeQuery(id+"F8.boolean.opBoolean","MERGE",EDGE,{"derivedFrom":[makeQuery(id+"F1.opExtrude","SWEPT_EDGE",EDGE,{"disambiguationData":[OSD([subQ1,subQ0])]}),makeQuery(id+"F8.opExtrude","SWEPT_EDGE",EDGE,{"disambiguationData":[OSD([subQ1,subQ0])]})]});}
            var Q2;
            {var subQ0=sQuery(id+"F0.wireOp",EDGE,"E5");var subQ1=sQuery(id+"F0.wireOp",EDGE,"E3");Q2=makeQuery(id+"F8.boolean.opBoolean","MERGE",EDGE,{"derivedFrom":[makeQuery(id+"F1.opExtrude","SWEPT_EDGE",EDGE,{"disambiguationData":[OSD([subQ1,subQ0])]}),makeQuery(id+"F8.opExtrude","SWEPT_EDGE",EDGE,{"disambiguationData":[OSD([subQ1,subQ0])]})]});}
            var Q3;
            {var subQ0=sQuery(id+"F0.wireOp",EDGE,"E4");var subQ1=sQuery(id+"F0.wireOp",EDGE,"E0");Q3=makeQuery(id+"F8.boolean.opBoolean","MERGE",EDGE,{"derivedFrom":[makeQuery(id+"F1.opExtrude","SWEPT_EDGE",EDGE,{"disambiguationData":[OSD([subQ1,subQ0])]}),makeQuery(id+"F8.opExtrude","SWEPT_EDGE",EDGE,{"disambiguationData":[OSD([subQ1,subQ0])]})]});}
            chamfer(context, id + "F13", {"entities" : qUnion([Q0, Q1, Q2, Q3]), "width" : 1 * mm, "tangentPropagation" : true});
        }
        {
            var Q0;
            Q0=makeQuery(id+"F10.boolean.opBoolean","COPY",FACE,{"derivedFrom":makeQuery(id+"F10.opExtrude","CAP_FACE",FACE,{"disambiguationData":[OSD([sQuery(id+"F0.wireOp",EDGE,"E40"),sQuery(id+"F0.wireOp",EDGE,"E41"),sQuery(id+"F0.wireOp",EDGE,"E42"),sQuery(id+"F0.wireOp",EDGE,"E43"),sQuery(id+"F0.wireOp",EDGE,"E44.MirrorCS"),sQuery(id+"F0.wireOp",EDGE,"E45.MirrorCS"),sQuery(id+"F0.wireOp",EDGE,"E46.MirrorCS"),sQuery(id+"F0.wireOp",EDGE,"E47.MirrorCS"),sQuery(id+"F0.wireOp",EDGE,"E48.filletArc"),sQuery(id+"F0.wireOp",EDGE,"E49.filletArc"),sQuery(id+"F0.wireOp",EDGE,"E50.filletArc"),sQuery(id+"F0.wireOp",EDGE,"E51.filletArc")])],"isStart":true})});
            var Q1;
            Q1=makeQuery(id+"F10.boolean.opBoolean","COPY",FACE,{"derivedFrom":makeQuery(id+"F10.opExtrude","CAP_FACE",FACE,{"disambiguationData":[OSD([sQuery(id+"F0.wireOp",EDGE,"E61"),sQuery(id+"F0.wireOp",EDGE,"E62"),sQuery(id+"F0.wireOp",EDGE,"E63"),sQuery(id+"F0.wireOp",EDGE,"E64"),sQuery(id+"F0.wireOp",EDGE,"E65.MirrorCS"),sQuery(id+"F0.wireOp",EDGE,"E66.MirrorCS"),sQuery(id+"F0.wireOp",EDGE,"E67.MirrorCS"),sQuery(id+"F0.wireOp",EDGE,"E68.MirrorCS"),sQuery(id+"F0.wireOp",EDGE,"E69.filletArc"),sQuery(id+"F0.wireOp",EDGE,"E70.filletArc"),sQuery(id+"F0.wireOp",EDGE,"E71.filletArc"),sQuery(id+"F0.wireOp",EDGE,"E72.filletArc")])],"isStart":true})});
            extrude(context, id + "F14", {"entities" : qUnion([Q0, Q1]), "operationType" : NewBodyOperationType.ADD, "depth" : 1.5 * mm, "offsetDistance" : 25 * mm});
        }
        {
            var Q0;
            Q0=makeQuery(id+"F4.opExtrude","CAP_FACE",FACE,{"disambiguationData":[OSD([sQuery(id+"F0.wireOp",EDGE,"E6"),sQuery(id+"F0.wireOp",EDGE,"E7"),sQuery(id+"F0.wireOp",EDGE,"E8"),sQuery(id+"F0.wireOp",EDGE,"E9"),sQuery(id+"F0.wireOp",EDGE,"E10"),sQuery(id+"F0.wireOp",EDGE,"E11"),sQuery(id+"F0.wireOp",EDGE,"E73"),sQuery(id+"F0.wireOp",EDGE,"E74"),sQuery(id+"F0.wireOp",EDGE,"E78"),sQuery(id+"F0.wireOp",EDGE,"E79"),sQuery(id+"F0.wireOp",EDGE,"E80.MirrorCS"),sQuery(id+"F0.wireOp",EDGE,"E81.MirrorCS")])],"isStart":true});
            var sketch = newSketch(context, id + "F15", { "sketchPlane" : qUnion([Q0])});
            skCircle(sketch, "E82", {"center": v(0, 0) * mm, "radius": 3.1 * mm});
            skCircle(sketch, "E83", {"center": v(0, 0) * mm, "radius": 3.85 * mm});
            skSolve(sketch);
        }
        {
            var Q0;
            Q0=makeQuery(id+"F15.imprint","IMPRINT",FACE,{"disambiguationData":[TD([[makeQuery(id+"F15.imprint","IMPRINT",EDGE,{"derivedFrom":sQuery(id+"F15.wireOp",EDGE,"E82")}),1.0]])]});
            extrude(context, id + "F16", {"entities" : qUnion([Q0]), "operationType" : NewBodyOperationType.REMOVE, "oppositeDirection" : true, "depth" : 2 * mm, "offsetDistance" : 25 * mm});
        }
        {
            var Q0;
            Q0=qCreatedBy(makeId("Right.planeOp"),FACE);
            var sketch = newSketch(context, id + "F17", { "sketchPlane" : qUnion([Q0])});
            skLineSegment(sketch, "E84", {"start": v(9.37, 39) * mm, "end": v(9.37, 31) * mm});
            skLineSegment(sketch, "E85", {"start": v(9.37, 39) * mm, "end": v(5.17, 39) * mm});
            skLineSegment(sketch, "E86", {"start": v(5.17, 39) * mm, "end": v(1.17, 39) * mm});
            skLineSegment(sketch, "E87", {"start": v(1.17, 39) * mm, "end": v(1.17, 35) * mm});
            skLineSegment(sketch, "E88", {"start": v(1.17, 35) * mm, "end": v(5.17, 35) * mm});
            skLineSegment(sketch, "E89", {"start": v(5.17, 35) * mm, "end": v(5.17, 39) * mm});
            skLineSegment(sketch, "E90", {"start": v(1.17, 35) * mm, "end": v(1.17, 28) * mm});
            skLineSegment(sketch, "E91", {"start": v(1.17, 28) * mm, "end": v(5.17, 28) * mm});
            skLineSegment(sketch, "E92", {"start": v(5.17, 28) * mm, "end": v(5.17, 35) * mm});
            skSolve(sketch);
        }
        {
            var Q0;
            Q0=makeQuery(id+"F17.imprint","IMPRINT",FACE,{"disambiguationData":[TD([[makeQuery(id+"F17.imprint","IMPRINT",EDGE,{"derivedFrom":sQuery(id+"F17.wireOp",EDGE,"E88")}),-1.0]])]});
            extrude(context, id + "F18", {"entities" : qUnion([Q0]), "operationType" : NewBodyOperationType.REMOVE, "depth" : 25 * mm, "offsetDistance" : 25 * mm});
        }
    });
